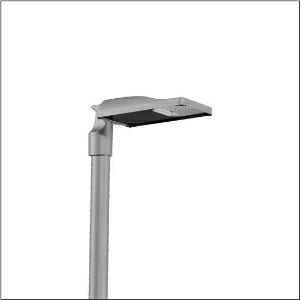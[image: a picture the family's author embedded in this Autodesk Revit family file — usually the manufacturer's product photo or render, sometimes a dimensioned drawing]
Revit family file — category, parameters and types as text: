
# Revit family: streetlight_sl_31_micro___st1_0a_5xh5d31b08ca_2a78
name_source: partatom
category: Lighting Fixtures
units: mm (PartAtom-declared; Revit-internal decimal feet)

## family parameters
Cut with Voids When Loaded = No
Host = Face
Light Source = No
Part Type = Normal
Room Calculation Point = No
Round Connector Dimension = Use Diameter
Shared = No

## types (1)
- --- (1 x LED, 1440 lm, 10.3 W, 3000K)
    Apparent Load = 10 VA
    CIE Flux Codes = 37 72 97 100 100
    Color Rendering = 70
    Color Temperature = 3000K
    Default Elevation = 1800 mm
    Description = Streetlight SL 31 micro Easy, LST, Desk-Remote mast luminaire for post-top, side-entry; light control with lens of PMMA; light distribution: ST1.0a, direct asymmetric distribution, for standard-compliant lighting for roads and squares; LED: luminous flux: 1.440lm, light colour: 730, colour temperature: 3000K; luminous efficacy: 139,8lm/W; control: pre-setting: linear dimming characteristic, flexible luminous flux parameterisation, time-dependent luminous flux control, constant luminous flux control, power reduction, intelligent temperature release in ECG and LED module, overheat protection; luminaire housing, of diecast aluminium, SITECO metallic grey (DB 702S), corrosivity category C5 high according to DIN EN ISO 12944; cover of toughened safety glass, transparent, opened without tools; mast flange of diecast aluminium, SITECO metallic grey (DB 702S), spigot size: 76/60mm, mast flange included unmounted; cable length: 5,5m, connection cable pre-assembled; mains connection: 220..240V, AC, 50/60Hz; power consumption (at start of service life): 10,3W / (at end of service life): 10,6W / (with reduced operation 50%): 5,3W; protection rating (complete): IP66; insulation class (complete): insulation class II (safety insulation); impact resistance: IK10; certification: CE, ENEC, ENEC+, VDE, UKCA; permissible operating ambient temperature for outdoor applications: -40..+50°C; packaging unit: 1 piece

Light Distribution: ST1.0a
    Height = 76 mm
    Lamp = 1 x LED
    Lamp Light Flux = 1440 lm
    Lamp Power = 10.3 W
    Lamp count = 1
    Length = 467 mm
    Luminous efficacy = 140 lm/W
    Manufacturer = Siteco
    ModVariant = No
    Model = 5XH5D31B08CA
    Number of Poles = 1
    OnlyDefault = Yes
    Power Factor = 1
    Product Name = Streetlight SL 31 micro | ST1.0a
    Product group = mast luminaire | pylon top
    ProductGroupID = 6100
    Protection Class = Protection class II
    Protection Degree = IP 66
    RLX_Detail_Level = 1
    RLX_Emergency_Light_Flux = 0 lm
    RLX_Emergency_Type = 0
    RLX_Emergency_Type_DB = No
    RlxData = <blob elided: 70393 chars, md5=4f1a2e78>
    Socket = socket
    Standby Power = 0 W
    System Light Flux = 1440 lm
    System Power = 10 W
    Type Comments = factory setting: luminous flux: 100 % | dim-lin: 254 | 386 mA
    Type Image = l_1300309.jpg
    URL = http://relux.com
    VarID = @adj_054305
    Voltage = 0 V
    Weight = 0.00 kg
    Width = 265 mm

## geometry (parser evidence)
native form markers: Blend x4, Sweep x9
no freeform markers — native parametric forms only
